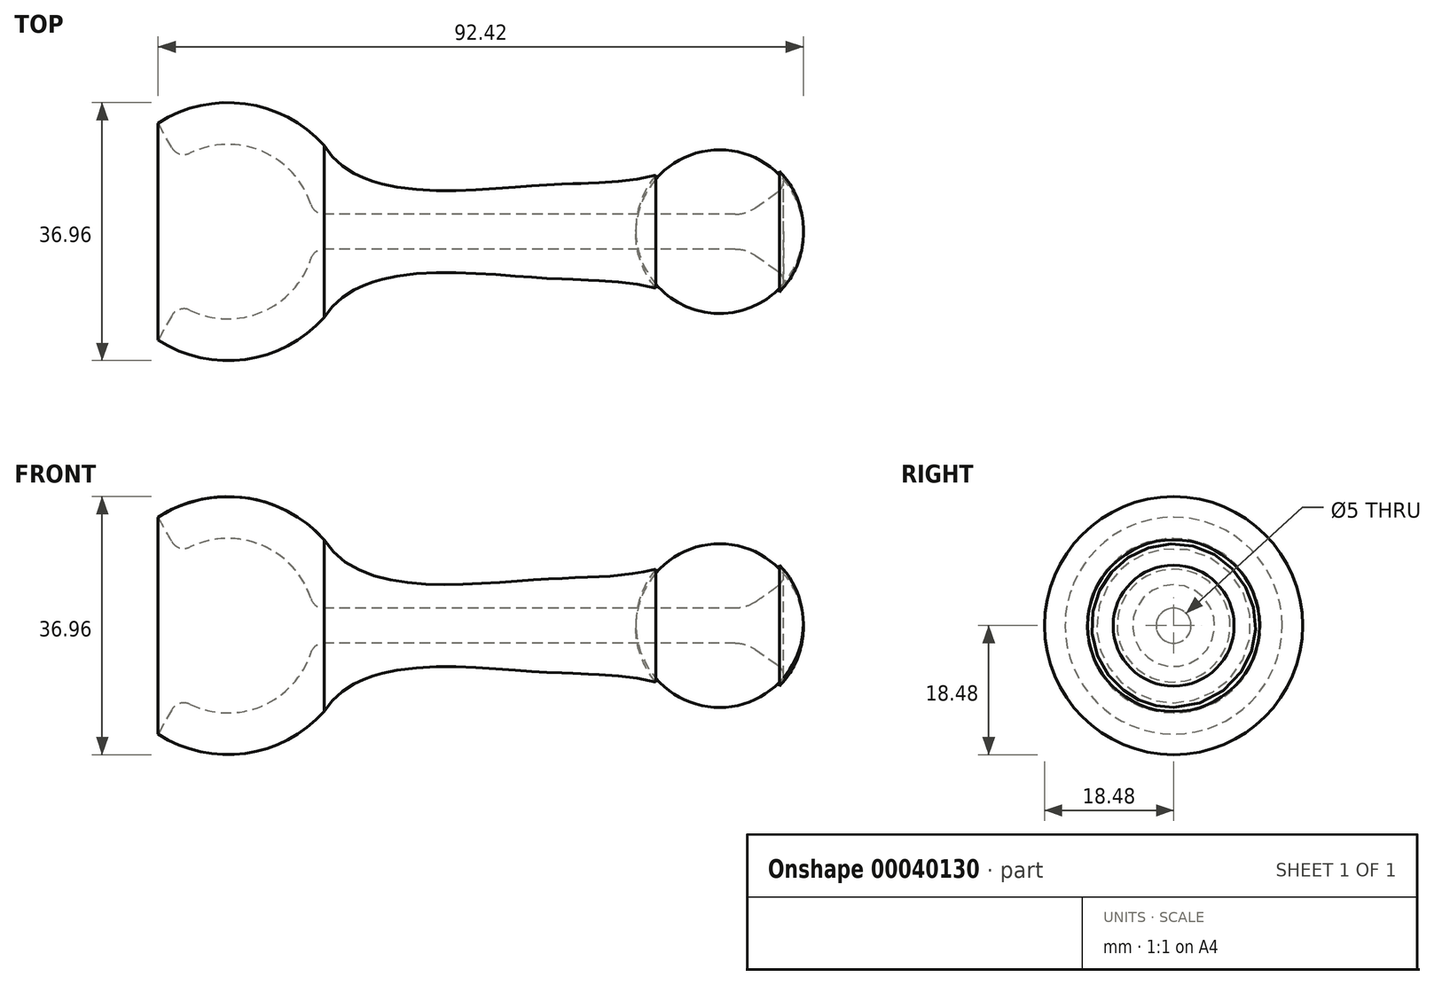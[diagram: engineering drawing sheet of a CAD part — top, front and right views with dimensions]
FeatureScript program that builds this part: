
annotation { "Feature Type Name" : "Feature", "Feature Type Description" : "" }
export const myFeature = defineFeature(function(context is Context, id is Id, definition is map)
    precondition{}
    {
        {
            var Q0;
            Q0=qCreatedBy(makeId("Front.planeOp"),FACE);
            var sketch = newSketch(context, id + "F0", { "sketchPlane" : qUnion([Q0])});
            skLineSegment(sketch, "E0", {"start": v(12.5, 0) * mm, "end": v(57.5, 0) * mm});
            skArc(sketch, "E1", {"start": v(12.25, 2.5) * mm, "mid": v(4.69, 11.59) * mm, "end": v(-7.07, 10.3) * mm});
            skFitSpline(sketch, "E2", {"points": [v(13.78, 12.32) * mm, v(44.08, 6.6) * mm, v(61.3, 8.08) * mm], "startDerivative": vector(27.08, -44.66) * mm, "endDerivative": vector(40.46, 9.5) * mm});
            skLineSegment(sketch, "E3", {"start": v(12.25, 2.5) * mm, "end": v(74.25, 2.5) * mm});
            skLineSegment(sketch, "E4", {"start": v(74.25, 2.5) * mm, "end": v(80.46, 6.85) * mm});
            skArc(sketch, "E5.trimOffspring", {"start": v(80.46, 6.85) * mm, "mid": v(71.19, 12.25) * mm, "end": v(61.3, 8.08) * mm});
            skPoint(sketch, "E6.end.orphan", {"position": v(82.25, 2.5) * mm});
            skPoint(sketch, "E7.orphan", {"position": v(82.5, 0) * mm});
            skArc(sketch, "E8", {"start": v(13.78, 12.32) * mm, "mid": v(2.48, 18.32) * mm, "end": v(-10, 15.54) * mm});
            skLineSegment(sketch, "E9", {"start": v(-7.07, 10.3) * mm, "end": v(-10, 15.54) * mm});
            skSolve(sketch);
        }
        {
            var Q0;
            Q0=makeQuery(id+"F0.imprint","IMPRINT",FACE,{"disambiguationData":[TD([[makeQuery(id+"F0.imprint","IMPRINT",EDGE,{"derivedFrom":sQuery(id+"F0.wireOp",EDGE,"E1")}),-1.0]])]});
            var Q1;
            Q1=sQuery(id+"F0.wireOp",EDGE,"E0");
            revolve(context, id + "F1", {"entities" : qUnion([Q0]), "axis" : qUnion([Q1]), "revolveType" : RevolveType.FULL});
        }
        {
            var Q0;
            Q0=makeQuery(id+"F1.opRevolve","SWEPT_EDGE",EDGE,{"disambiguationData":[OSD([sQuery(id+"F0.wireOp",EDGE,"E1"),sQuery(id+"F0.wireOp",EDGE,"CbFEBDJi-CplH-pibZ-NPAv-z09MQRNn6UNR")])]});
            var Q1;
            Q1=makeQuery(id+"F1.opRevolve","SWEPT_EDGE",EDGE,{"disambiguationData":[OSD([sQuery(id+"F0.wireOp",EDGE,"E4"),sQuery(id+"F0.wireOp",EDGE,"E5.trimOffspring")])]});
            fillet(context, id + "F2", {"entities" : qUnion([Q0, Q1]), "radius" : 2 * mm, "tangentPropagation" : true, "allowEdgeOverflow" : false});
        }
        {
            var Q0;
            Q0=makeQuery(id+"F1.opRevolve","SWEPT_EDGE",EDGE,{"disambiguationData":[OSD([sQuery(id+"F0.wireOp",EDGE,"E3"),sQuery(id+"F0.wireOp",EDGE,"E4")])]});
            fillet(context, id + "F3", {"entities" : qUnion([Q0]), "radius" : 5 * mm, "tangentPropagation" : true, "allowEdgeOverflow" : false});
        }
    });
